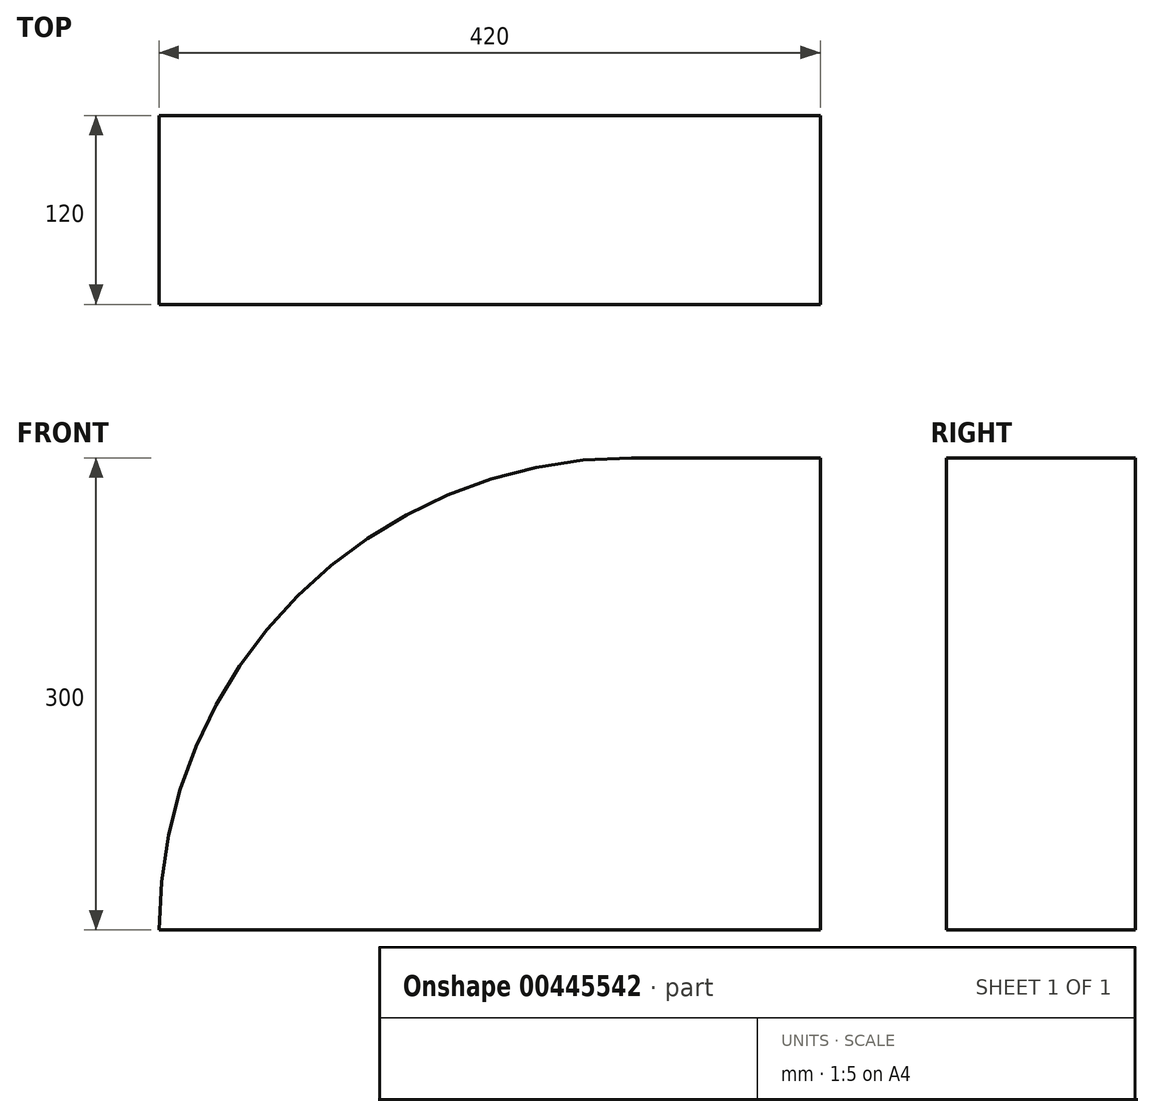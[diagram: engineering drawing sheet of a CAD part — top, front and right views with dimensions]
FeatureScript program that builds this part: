
annotation { "Feature Type Name" : "Feature", "Feature Type Description" : "" }
export const myFeature = defineFeature(function(context is Context, id is Id, definition is map)
    precondition{}
    {
        {
            var Q0;
            Q0=qCreatedBy(makeId("Front.planeOp"),FACE);
            var sketch = newSketch(context, id + "F0", { "sketchPlane" : qUnion([Q0])});
            skLineSegment(sketch, "E0.top", {"start": v(0, 0) * mm, "end": v(0, 300) * mm});
            skLineSegment(sketch, "E0.left", {"start": v(-420, 0) * mm, "end": v(0, 0) * mm});
            skLineSegment(sketch, "E0.right", {"start": v(-120, 300) * mm, "end": v(0, 300) * mm});
            skArc(sketch, "E1", {"start": v(-120, 300) * mm, "mid": v(-332.13, 212.13) * mm, "end": v(-420, 0) * mm});
            skLineSegment(sketch, "E2", {"start": v(-420, 0) * mm, "end": v(-420, 300) * mm, "construction": true});
            skSolve(sketch);
        }
        {
            var Q0;
            Q0 = qSketchRegion(id + "F0", true);
            extrude(context, id + "F1", {"entities" : qUnion([Q0]), "depth" : 120 * mm});
        }
        {
            var Q0;
            Q0=makeQuery(id+"F1.opExtrude","CAP_FACE",FACE,{"disambiguationData":[OSD([sQuery(id+"F0.wireOp",EDGE,"E0.top"),sQuery(id+"F0.wireOp",EDGE,"E0.left"),sQuery(id+"F0.wireOp",EDGE,"E0.right"),sQuery(id+"F0.wireOp",EDGE,"E1")])],"isStart":false});
            var sketch = newSketch(context, id + "F2", { "sketchPlane" : qUnion([Q0])});
            skCircle(sketch, "E3", {"center": v(-231.78, 145.4) * mm, "radius": 82.7 * mm});
            skSolve(sketch);
        }
        {
            var Q0;
            Q0 = qSketchRegion(id + "F2", true);
            extrude(context, id + "F3", {"entities" : qUnion([Q0]), "operationType" : NewBodyOperationType.REMOVE, "depth" : 25 * mm});
        }
    });
